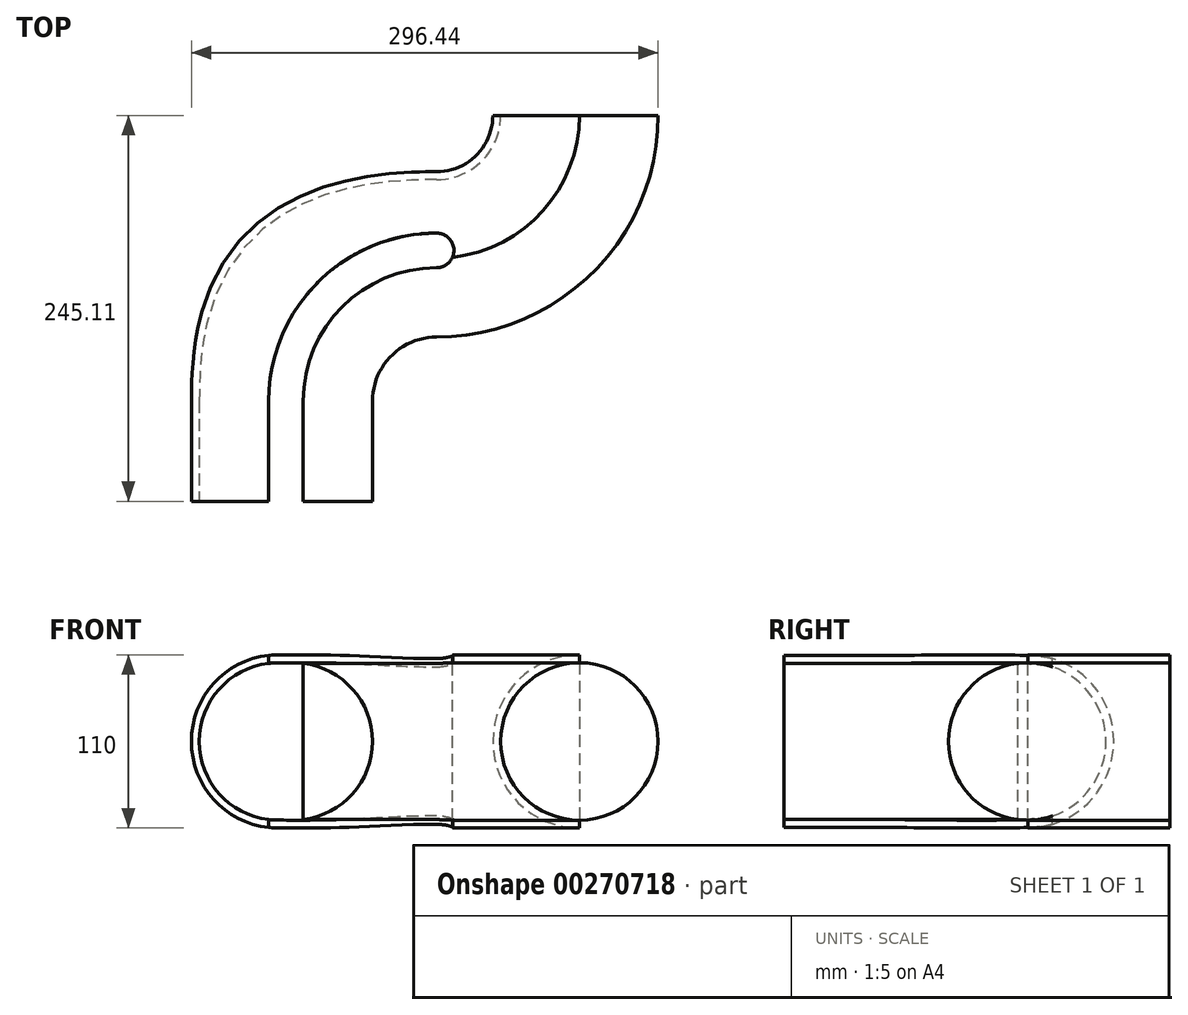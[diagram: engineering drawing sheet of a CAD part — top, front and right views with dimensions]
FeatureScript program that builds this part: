
annotation { "Feature Type Name" : "Feature", "Feature Type Description" : "" }
export const myFeature = defineFeature(function(context is Context, id is Id, definition is map)
    precondition{}
    {
        {
            var Q0;
            Q0=qCreatedBy(makeId("Top.planeOp"),FACE);
            var sketch = newSketch(context, id + "F0", { "sketchPlane" : qUnion([Q0])});
            skArc(sketch, "E0", {"start": v(0, 0) * mm, "mid": v(-26.57, -64.15) * mm, "end": v(-90.72, -90.72) * mm});
            skLineSegment(sketch, "E1", {"start": v(-90.72, 0) * mm, "end": v(-90.72, -90.72) * mm, "construction": true});
            skLineSegment(sketch, "E2", {"start": v(-90.72, 0) * mm, "end": v(0, 0) * mm, "construction": true});
            skLineSegment(sketch, "E3", {"start": v(-90.72, -90.72) * mm, "end": v(-34.94, -90.72) * mm, "construction": true});
            skArc(sketch, "E4", {"start": v(-90.72, -90.72) * mm, "mid": v(-154.87, -117.3) * mm, "end": v(-181.44, -181.44) * mm});
            skLineSegment(sketch, "E5", {"start": v(-181.44, -181.44) * mm, "end": v(-90.72, -181.44) * mm, "construction": true});
            skLineSegment(sketch, "E6", {"start": v(-90.72, -90.72) * mm, "end": v(-90.72, -181.44) * mm, "construction": true});
            skLineSegment(sketch, "E7", {"start": v(-181.44, -181.44) * mm, "end": v(-181.44, -245.1) * mm});
            skLineSegment(sketch, "E8.0", {"start": v(-191.44, -181.44) * mm, "end": v(-191.44, -245.1) * mm});
            skFitSpline(sketch, "E9", {"points": [v(-90.72, -90.72) * mm, v(-191.44, -181.44) * mm], "startDerivative": vector(-276.12, 0.71) * mm, "endDerivative": vector(-1.04, -151.65) * mm});
            skLineSegment(sketch, "E10", {"start": v(-181.44, -245.1) * mm, "end": v(-191.44, -245.1) * mm});
            skLineSegment(sketch, "E11.0", {"start": v(-186.44, -181.44) * mm, "end": v(-186.44, -245.1) * mm});
            skArc(sketch, "E11.1", {"start": v(-90.72, -85.72) * mm, "mid": v(-158.4, -113.76) * mm, "end": v(-186.44, -181.44) * mm});
            skArc(sketch, "E12.0.startCap", {"start": v(-90.72, -74.72) * mm, "mid": v(-79.72, -85.72) * mm, "end": v(-90.72, -96.72) * mm});
            skArc(sketch, "E12.0.left", {"start": v(-90.72, -96.72) * mm, "mid": v(-150.63, -121.54) * mm, "end": v(-175.44, -181.44) * mm});
            skArc(sketch, "E12.0.right", {"start": v(-90.72, -74.72) * mm, "mid": v(-166.19, -105.98) * mm, "end": v(-197.44, -181.44) * mm});
            skArc(sketch, "E12.1.endCap", {"start": v(-175.44, -245.1) * mm, "mid": v(-186.44, -256.1) * mm, "end": v(-197.44, -245.1) * mm});
            skLineSegment(sketch, "E12.1.left", {"start": v(-175.44, -181.44) * mm, "end": v(-175.44, -245.1) * mm});
            skLineSegment(sketch, "E12.1.right", {"start": v(-197.44, -181.44) * mm, "end": v(-197.44, -245.1) * mm});
            skSolve(sketch);
        }
        {
            var Q0;
            Q0=qCreatedBy(makeId("Front.planeOp"),FACE);
            var sketch = newSketch(context, id + "F1", { "sketchPlane" : qUnion([Q0])});
            skArc(sketch, "E13", {"start": v(0, 50) * mm, "mid": v(-50, 0) * mm, "end": v(0, -50) * mm});
            skArc(sketch, "E14.MirrorCS", {"start": v(0, 50) * mm, "mid": v(50, 0) * mm, "end": v(0, -50) * mm});
            skArc(sketch, "E15.0", {"start": v(0, 55) * mm, "mid": v(-55, 0) * mm, "end": v(0, -55) * mm});
            skArc(sketch, "E16.MirrorCS", {"start": v(0, 55) * mm, "mid": v(55, 0) * mm, "end": v(0, -55) * mm});
            skLineSegment(sketch, "E17", {"start": v(0, 55) * mm, "end": v(0, -55) * mm});
            skSolve(sketch);
        }
        {
            var Q0;
            {var subQ0=sQuery(id+"F1.wireOp",EDGE,"E14.MirrorCS");Q0=makeQuery(id+"F1.imprint","IMPRINT",FACE,{"disambiguationData":[TD([[makeQuery(id+"F1.imprint","IMPRINT",EDGE,{"derivedFrom":subQ0}),1.0]])]});}
            var Q1;
            Q1=sQuery(id+"F0.wireOp",EDGE,"E0");
            var Q2;
            Q2=sQuery(id+"F0.wireOp",EDGE,"E4");
            var Q3;
            Q3=sQuery(id+"F0.wireOp",EDGE,"E7");
            sweep(context, id + "F2", {"profiles" : qUnion([Q0]), "path" : qUnion([Q1, Q2, Q3])});
        }
        {
            var Q0;
            {var subQ0=sQuery(id+"F1.wireOp",EDGE,"E13");Q0=makeQuery(id+"F1.imprint","IMPRINT",FACE,{"disambiguationData":[TD([[makeQuery(id+"F1.imprint","IMPRINT",EDGE,{"derivedFrom":subQ0}),-1.0]])]});}
            var Q1;
            Q1=sQuery(id+"F0.wireOp",EDGE,"E0");
            var Q2;
            Q2=sQuery(id+"F0.wireOp",EDGE,"E9");
            var Q3;
            Q3=sQuery(id+"F0.wireOp",EDGE,"E8.0");
            sweep(context, id + "F3", {"operationType" : NewBodyOperationType.ADD, "profiles" : qUnion([Q0]), "path" : qUnion([Q1, Q2, Q3])});
        }
        {
            var Q0;
            {var subQ5=sQuery(id+"F0.wireOp",EDGE,"E4");Q0=makeQuery(id+"F0.imprint","IMPRINT",FACE,{"disambiguationData":[TD([[makeQuery(id+"F0.imprint","IMPRINT",EDGE,{"derivedFrom":subQ5}),1.0]])]});}
            extrude(context, id + "F4", {"entities" : qUnion([Q0]), "operationType" : NewBodyOperationType.REMOVE, "endBound" : BoundingType.THROUGH_ALL, "oppositeDirection" : true, "depth" : 25 * mm, "hasSecondDirection" : true, "secondDirectionBound" : SecondDirectionBoundingType.THROUGH_ALL, "secondDirectionOppositeDirection" : false, "secondDirectionDepth" : 25 * mm});
        }
    });
